# Revit family: 604406091_Mueble Aluvia Habano 60x45
name_source: partatom
category: Generic Models
units: mm (PartAtom-declared; Revit-internal decimal feet)

## family parameters
Always vertical = Yes
Can host rebar = No
Cut with Voids When Loaded = No
Host = Wall
OmniClass Number = 23.31.13.11
OmniClass Title = Single Sinks
Part Type = Normal
Room Calculation Point = No
Round Connector Dimension = Use Diameter
Shared = No

## types (2) — shared parameters
Alto = 850 mm  [stored 2.78871 ft]
Ancho = 595 mm
Canto = PVC rígido 2 mm de calibre.
PVC Flexible 0,5 mm de calibre.
Carga Máxima = 110,2 lb (50 kg).
Creado por = IDD
Densidad = 15mm 670 kg./m^3.
Description = La línea ALUVIA viene a entregar de manera asequible una solución perfecta que combina
diseño y funcionalidad, ALUVIA se inspira en el movimiento y caída del agua en la
naturaleza, es por ello de sus formas orgánicas donde podemos obtener un producto
compacto y de líneas fluidas, que se adapta en espacios pequeños.
· Mueble compacto para espacios pequeños.
· Lavamanos 100% en porcelana.
· Grán capacidad de almacenamiento.
· Resistentes a la Humedad.
Dimensiones Generales (H* W * P) = 33,46” x 23,43” x 17,52” (850 x 595 x 445 mm).
Fecha de creación = 21/07/2020
Garantía Herrajes = 1 año
Garantía Madera = 1 año
Manufacturer = Corona
Peso Bruto aprox = 49,4 lb (22,4 kg).
Peso Neto aprox = 46,7 lb (21,2 kg).
Profundidad = 445 mm  [stored 1.45997 ft]
Resistencia a la humedad = 8%.
Resistencia al rayado = 700 ciclos.
Textura = Habano: Poro - Gris: Soft.
Tiempo de Armado = 80 Minutos.
URL = https://corona.co

## per-type parameters (varying)
| type | Material | Material Pieza en U | Material Piezas interiores | Material patas |
| Type 1 | <By Category> | <By Category> | <By Category> | <By Category> |
| Ref. 604406091 Mueble Aluvia Habano Con Lavamanos. | Corona_Madera_Aglomerada_Habano | Corona_Acero | Corona_Madera_Aglomerada_Plomo | Corona_Acero |

note: [stored X ft] marks values corroborated as IEEE doubles in the binary element streams (Revit-internal decimal feet)

## geometry (parser evidence)
native form markers: Sweep x7
no freeform markers — native parametric forms only
